# Revit family: Tables-Casual-Teknion-ATCCL_Circular_Lounge-R20151
name_source: partatom
category: Furniture
revit_build: Autodesk Revit Architecture 2015 (Build: 20140323_1530(x64)
units: mm (PartAtom-declared; Revit-internal decimal feet)

## types (2) — shared parameters
Assembly Code = E2020200
Manufacturer = Teknion
Manufacturer Fax = 416.661.4586
Part Number = ATCCL
Product Documentation Link = https://www.teknion.com
Product Line = Tables & Collaborative Spaces
Product Page URL = https://www.teknion.com
Series = Tables & Collaborative Spaces
Sustainability Data = http://www.teknion.com
URL = www.teknion.com
Unit Weight URL = http://www.teknion.com
Warranty = http://www.teknion.com

## per-type parameters (varying)
| type | Description | Model | Width |
| 24" Diameter | Circular Lounge Table, 24" Diameter | ATCCL24 | 24 " |
| 30" Diameter | Circular Lounge Table, 30" Diameter | ATCCL30 | 30 " |

## geometry (parser evidence)
native form markers: Sweep x3
no freeform markers — native parametric forms only
